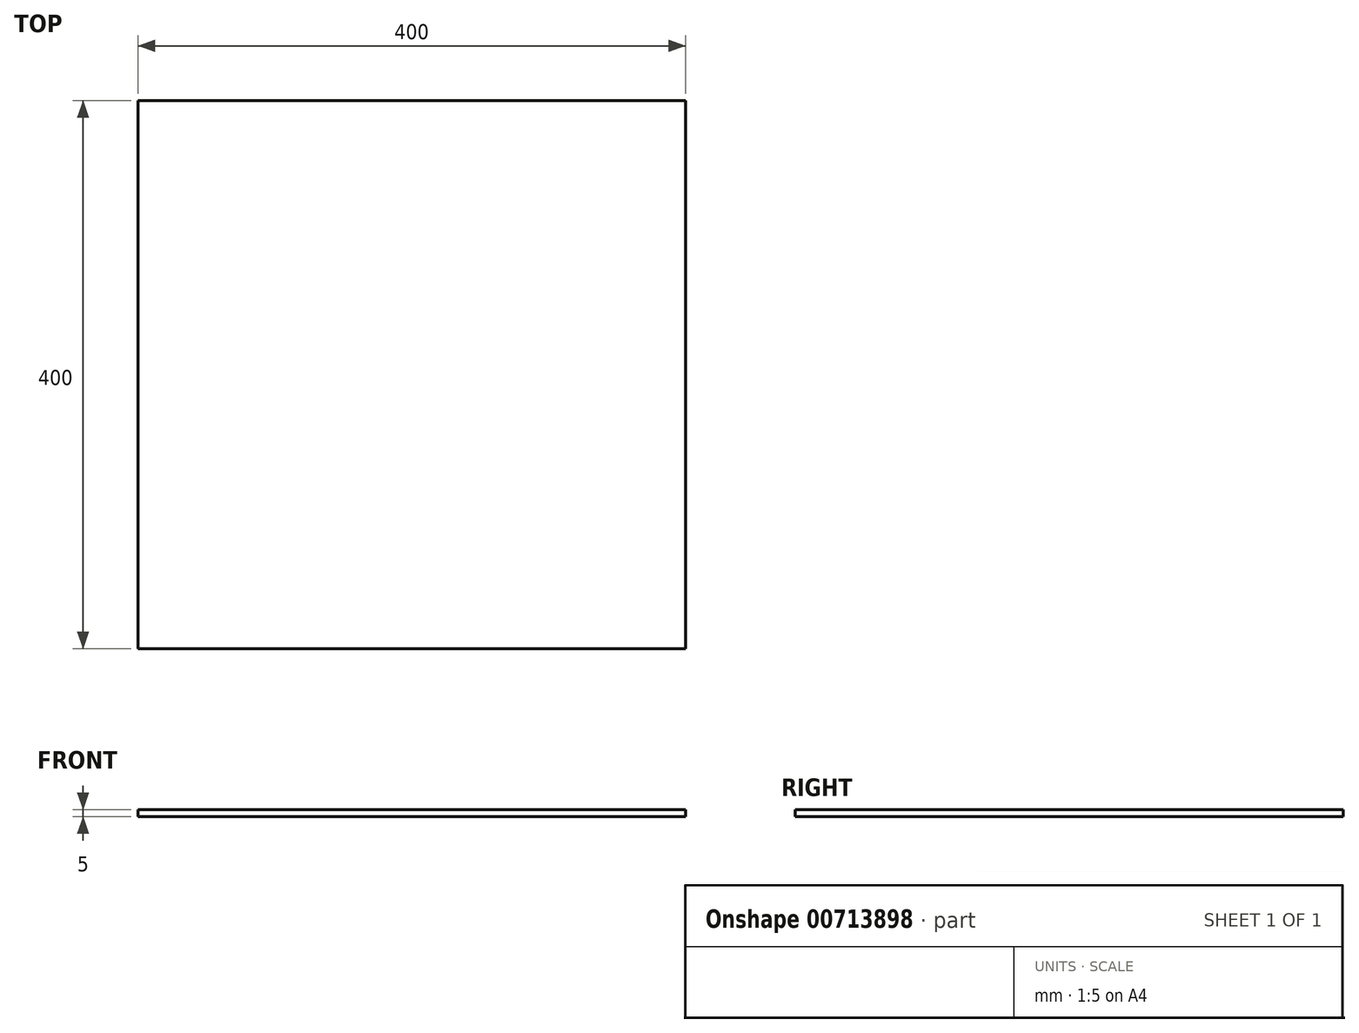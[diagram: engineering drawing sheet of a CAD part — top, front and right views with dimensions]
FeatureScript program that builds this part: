
annotation { "Feature Type Name" : "Feature", "Feature Type Description" : "" }
export const myFeature = defineFeature(function(context is Context, id is Id, definition is map)
    precondition{}
    {
        {
            var Q0;
            Q0=qCreatedBy(makeId("Top.planeOp"),FACE);
            var sketch = newSketch(context, id + "F0", { "sketchPlane" : qUnion([Q0])});
            skLineSegment(sketch, "E0.bottom", {"start": v(-48.98, -42.43) * mm, "end": v(351.02, -42.43) * mm});
            skLineSegment(sketch, "E0.top", {"start": v(-48.98, 357.57) * mm, "end": v(351.02, 357.57) * mm});
            skLineSegment(sketch, "E0.left", {"start": v(-48.98, -42.43) * mm, "end": v(-48.98, 357.57) * mm});
            skLineSegment(sketch, "E0.right", {"start": v(351.02, -42.43) * mm, "end": v(351.02, 357.57) * mm});
            skSolve(sketch);
        }
        {
            var Q0;
            Q0=makeQuery(id+"F0.imprint","IMPRINT",FACE,{"disambiguationData":[TD([[makeQuery(id+"F0.imprint","IMPRINT",EDGE,{"derivedFrom":sQuery(id+"F0.wireOp",EDGE,"E0.bottom")}),1.0]])]});
            extrude(context, id + "F1", {"entities" : qUnion([Q0]), "depth" : 5 * mm, "offsetDistance" : 25 * mm});
        }
    });
